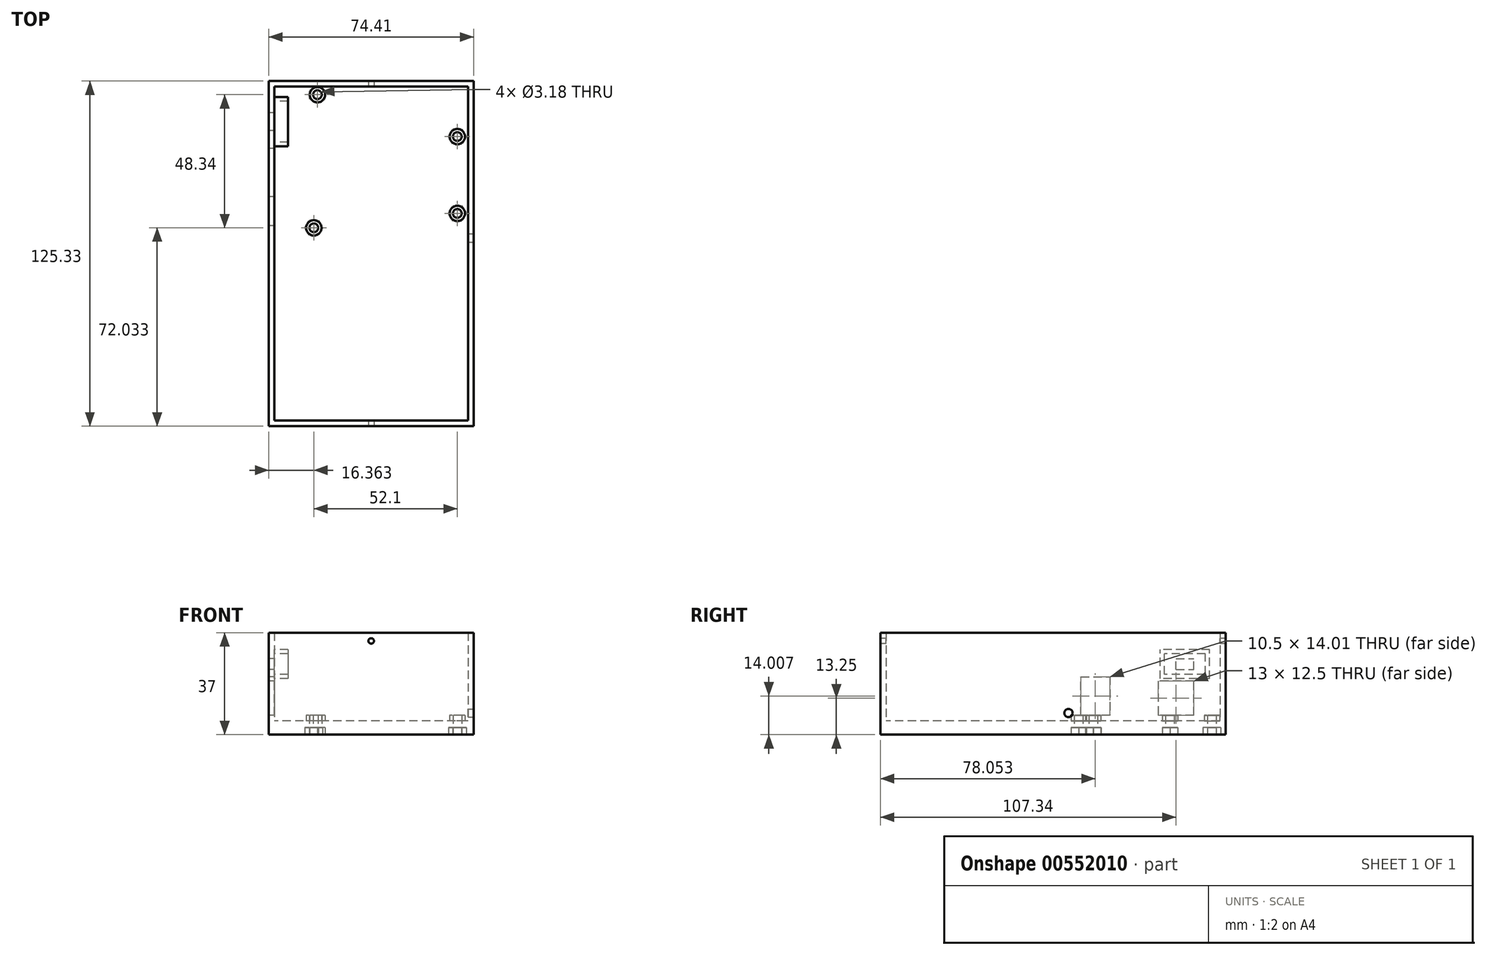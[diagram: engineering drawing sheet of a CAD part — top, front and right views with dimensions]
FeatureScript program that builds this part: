
annotation { "Feature Type Name" : "Feature", "Feature Type Description" : "" }
export const myFeature = defineFeature(function(context is Context, id is Id, definition is map)
    precondition{}
    {
        {
            var Q0;
            Q0=qCreatedBy(makeId("Top.planeOp"),FACE);
            var sketch = newSketch(context, id + "F0", { "sketchPlane" : qUnion([Q0])});
            skLineSegment(sketch, "E0.right", {"start": v(-46.5, 29) * mm, "end": v(-46.5, -29) * mm});
            skPoint(sketch, "E0.middle", {"position": v(0, 0) * mm});
            skCircle(sketch, "E1", {"center": v(-30.14, -24.3) * mm, "radius": 1.59 * mm});
            skCircle(sketch, "E2", {"center": v(21.96, -19.06) * mm, "radius": 1.59 * mm});
            skCircle(sketch, "E3", {"center": v(21.96, 8.84) * mm, "radius": 1.59 * mm});
            skCircle(sketch, "E4", {"center": v(-28.84, 24.04) * mm, "radius": 1.59 * mm});
            skLineSegment(sketch, "E5.left", {"start": v(-46.5, -29) * mm, "end": v(-46.5, -29) * mm});
            skLineSegment(sketch, "E6.right", {"start": v(-46.5, -29) * mm, "end": v(-46.5, -96.33) * mm});
            skLineSegment(sketch, "E7", {"start": v(27.91, 29) * mm, "end": v(27.91, -96.33) * mm});
            skLineSegment(sketch, "E8", {"start": v(-46.5, 29) * mm, "end": v(27.91, 29) * mm});
            skLineSegment(sketch, "E9", {"start": v(27.91, -96.33) * mm, "end": v(-46.5, -96.33) * mm});
            skSolve(sketch);
        }
        {
            var Q0;
            Q0=makeQuery(id+"F0.imprint","IMPRINT",FACE,{"disambiguationData":[TD([[makeQuery(id+"F0.imprint","IMPRINT",EDGE,{"derivedFrom":sQuery(id+"F0.wireOp",EDGE,"E0.bottom")}),1.0]])]});
            var Q1;
            Q1=makeQuery(id+"F0.imprint","IMPRINT",FACE,{"disambiguationData":[TD([[makeQuery(id+"F0.imprint","IMPRINT",EDGE,{"derivedFrom":sQuery(id+"F0.wireOp",EDGE,"E2")}),1.0]])]});
            var Q2;
            Q2=makeQuery(id+"F0.imprint","IMPRINT",FACE,{"disambiguationData":[TD([[makeQuery(id+"F0.imprint","IMPRINT",EDGE,{"derivedFrom":sQuery(id+"F0.wireOp",EDGE,"E4")}),1.0]])]});
            var Q3;
            Q3=makeQuery(id+"F0.imprint","IMPRINT",FACE,{"disambiguationData":[TD([[makeQuery(id+"F0.imprint","IMPRINT",EDGE,{"derivedFrom":sQuery(id+"F0.wireOp",EDGE,"E1")}),1.0]])]});
            var Q4;
            Q4=makeQuery(id+"F0.imprint","IMPRINT",FACE,{"disambiguationData":[TD([[makeQuery(id+"F0.imprint","IMPRINT",EDGE,{"derivedFrom":sQuery(id+"F0.wireOp",EDGE,"E3")}),1.0]])]});
            var Q5;
            Q5=makeQuery(id+"F0.imprint","IMPRINT",FACE,{"disambiguationData":[TD([[makeQuery(id+"F0.imprint","IMPRINT",EDGE,{"derivedFrom":sQuery(id+"F0.wireOp",EDGE,"E6.bottom")}),1.0]])]});
            var Q6;
            Q6=makeQuery(id+"F0.imprint","IMPRINT",FACE,{"disambiguationData":[TD([[makeQuery(id+"F0.imprint","IMPRINT",EDGE,{"derivedFrom":sQuery(id+"F0.wireOp",EDGE,"E0.right")}),1.0]])]});
            extrude(context, id + "F1", {"entities" : qUnion([Q0, Q1, Q2, Q3, Q4, Q5, Q6]), "depth" : 5 * mm, "offsetDistance" : 25 * mm});
        }
        {
            var Q0;
            Q0=makeQuery(id+"F1.opExtrude","CAP_FACE",FACE,{"disambiguationData":[OSD([sQuery(id+"F0.wireOp",EDGE,"E0.bottom"),sQuery(id+"F0.wireOp",EDGE,"E0.top"),sQuery(id+"F0.wireOp",EDGE,"E0.left"),sQuery(id+"F0.wireOp",EDGE,"E0.right"),sQuery(id+"F0.wireOp",EDGE,"E1"),sQuery(id+"F0.wireOp",EDGE,"E2"),sQuery(id+"F0.wireOp",EDGE,"E3"),sQuery(id+"F0.wireOp",EDGE,"E4")])],"isStart":false});
            var sketch = newSketch(context, id + "F2", { "sketchPlane" : qUnion([Q0])});
            skLineSegment(sketch, "E10.0", {"start": v(25.91, -94.33) * mm, "end": v(-44.5, -94.33) * mm});
            skLineSegment(sketch, "E10.1", {"start": v(25.91, 27) * mm, "end": v(25.91, -94.33) * mm});
            skLineSegment(sketch, "E10.2", {"start": v(-44.5, -29) * mm, "end": v(-44.5, -94.33) * mm});
            skLineSegment(sketch, "E10.3", {"start": v(-44.5, 27) * mm, "end": v(-44.5, -29) * mm});
            skLineSegment(sketch, "E10.4", {"start": v(-44.5, 27) * mm, "end": v(25.91, 27) * mm});
            skSolve(sketch);
        }
        {
            var Q0;
            Q0=makeQuery(id+"F2.imprint","IMPRINT",FACE,{"disambiguationData":[TD([[makeQuery(id+"F2.imprint","IMPRINT",EDGE,{"derivedFrom":sQuery(id+"F2.wireOp",EDGE,"E10.0")}),1.0]])]});
            extrude(context, id + "F3", {"entities" : qUnion([Q0]), "operationType" : NewBodyOperationType.ADD, "depth" : 32 * mm, "offsetDistance" : 25 * mm});
        }
        {
            var Q0;
            Q0=makeQuery(id+"F1.opExtrude","CAP_FACE",FACE,{"disambiguationData":[OSD([sQuery(id+"F0.wireOp",EDGE,"E0.bottom"),sQuery(id+"F0.wireOp",EDGE,"E0.top"),sQuery(id+"F0.wireOp",EDGE,"E0.left"),sQuery(id+"F0.wireOp",EDGE,"E0.right"),sQuery(id+"F0.wireOp",EDGE,"E1"),sQuery(id+"F0.wireOp",EDGE,"E2"),sQuery(id+"F0.wireOp",EDGE,"E3"),sQuery(id+"F0.wireOp",EDGE,"E4")])],"isStart":false});
            var sketch = newSketch(context, id + "F4", { "sketchPlane" : qUnion([Q0])});
            skCircle(sketch, "E11.0", {"center": v(-28.84, 24.04) * mm, "radius": 2.8 * mm});
            skCircle(sketch, "E12.0", {"center": v(21.96, 8.84) * mm, "radius": 2.79 * mm});
            skCircle(sketch, "E13.0", {"center": v(21.96, -19.06) * mm, "radius": 2.8 * mm});
            skCircle(sketch, "E14.0", {"center": v(-30.14, -24.3) * mm, "radius": 2.8 * mm});
            skSolve(sketch);
        }
        {
            var Q0;
            Q0 = qSketchRegion(id + "F4", true);
            extrude(context, id + "F5", {"entities" : qUnion([Q0]), "operationType" : NewBodyOperationType.ADD, "depth" : 2 * mm, "offsetDistance" : 25 * mm});
        }
        {
            var Q0;
            Q0=makeQuery(id+"F0.imprint","IMPRINT",FACE,{"disambiguationData":[TD([[makeQuery(id+"F0.imprint","IMPRINT",EDGE,{"derivedFrom":sQuery(id+"F0.wireOp",EDGE,"E1")}),1.0]])]});
            var Q1;
            Q1=makeQuery(id+"F0.imprint","IMPRINT",FACE,{"disambiguationData":[TD([[makeQuery(id+"F0.imprint","IMPRINT",EDGE,{"derivedFrom":sQuery(id+"F0.wireOp",EDGE,"E2")}),1.0]])]});
            var Q2;
            Q2=makeQuery(id+"F0.imprint","IMPRINT",FACE,{"disambiguationData":[TD([[makeQuery(id+"F0.imprint","IMPRINT",EDGE,{"derivedFrom":sQuery(id+"F0.wireOp",EDGE,"E3")}),1.0]])]});
            var Q3;
            Q3=makeQuery(id+"F0.imprint","IMPRINT",FACE,{"disambiguationData":[TD([[makeQuery(id+"F0.imprint","IMPRINT",EDGE,{"derivedFrom":sQuery(id+"F0.wireOp",EDGE,"E4")}),1.0]])]});
            var Q4;
            Q4=sQuery(id+"F0.wireOp",EDGE,"E1");
            var Q5;
            Q5=sQuery(id+"F0.wireOp",EDGE,"E2");
            var Q6;
            Q6=sQuery(id+"F0.wireOp",EDGE,"E3");
            var Q7;
            Q7=sQuery(id+"F0.wireOp",EDGE,"E4");
            extrude(context, id + "F6", {"entities" : qUnion([Q0, Q1, Q2, Q3]), "operationType" : NewBodyOperationType.REMOVE, "surfaceEntities" : qUnion([Q4, Q5, Q6, Q7]), "endBound" : BoundingType.THROUGH_ALL, "depth" : 25 * mm, "offsetDistance" : 25 * mm});
        }
        {
            var Q0;
            Q0=qCreatedBy(makeId("Top.planeOp"),FACE);
            var sketch = newSketch(context, id + "F7", { "sketchPlane" : qUnion([Q0])});
            skCircle(sketch, "E15.cCircle", {"center": v(-30.14, -24.3) * mm, "radius": 2.8 * mm, "construction": true});
            skLineSegment(sketch, "E15.0", {"start": v(-26.9, -24.32) * mm, "end": v(-28.54, -27.1) * mm});
            skLineSegment(sketch, "E15.1", {"start": v(-28.54, -27.1) * mm, "end": v(-31.77, -27.09) * mm});
            skLineSegment(sketch, "E15.2", {"start": v(-31.77, -27.09) * mm, "end": v(-33.37, -24.28) * mm});
            skLineSegment(sketch, "E15.3", {"start": v(-33.37, -24.28) * mm, "end": v(-31.73, -21.49) * mm});
            skLineSegment(sketch, "E15.4", {"start": v(-31.73, -21.49) * mm, "end": v(-28.5, -21.5) * mm});
            skLineSegment(sketch, "E15.5", {"start": v(-28.5, -21.5) * mm, "end": v(-26.9, -24.32) * mm});
            skPoint(sketch, "E15.0.midPoint", {"position": v(-27.72, -25.71) * mm});
            skCircle(sketch, "E16.cCircle", {"center": v(21.96, -19.06) * mm, "radius": 2.8 * mm, "construction": true});
            skLineSegment(sketch, "E16.0", {"start": v(25.2, -18.98) * mm, "end": v(23.65, -21.82) * mm});
            skLineSegment(sketch, "E16.1", {"start": v(23.65, -21.82) * mm, "end": v(20.42, -21.9) * mm});
            skLineSegment(sketch, "E16.2", {"start": v(20.42, -21.9) * mm, "end": v(18.73, -19.14) * mm});
            skLineSegment(sketch, "E16.3", {"start": v(18.73, -19.14) * mm, "end": v(20.28, -16.3) * mm});
            skLineSegment(sketch, "E16.4", {"start": v(20.28, -16.3) * mm, "end": v(23.5, -16.22) * mm});
            skLineSegment(sketch, "E16.5", {"start": v(23.5, -16.22) * mm, "end": v(25.2, -18.98) * mm});
            skPoint(sketch, "E16.0.midPoint", {"position": v(24.42, -20.4) * mm});
            skCircle(sketch, "E17.cCircle", {"center": v(21.96, 8.84) * mm, "radius": 2.8 * mm, "construction": true});
            skLineSegment(sketch, "E17.0", {"start": v(25.2, 8.84) * mm, "end": v(23.58, 6.04) * mm});
            skLineSegment(sketch, "E17.1", {"start": v(23.58, 6.04) * mm, "end": v(20.34, 6.05) * mm});
            skLineSegment(sketch, "E17.2", {"start": v(20.34, 6.05) * mm, "end": v(18.73, 8.85) * mm});
            skLineSegment(sketch, "E17.3", {"start": v(18.73, 8.85) * mm, "end": v(20.35, 11.65) * mm});
            skLineSegment(sketch, "E17.4", {"start": v(20.35, 11.65) * mm, "end": v(23.58, 11.64) * mm});
            skLineSegment(sketch, "E17.5", {"start": v(23.58, 11.64) * mm, "end": v(25.2, 8.84) * mm});
            skPoint(sketch, "E17.0.midPoint", {"position": v(24.39, 7.44) * mm});
            skCircle(sketch, "E18.cCircle", {"center": v(-28.84, 24.04) * mm, "radius": 3.23 * mm, "construction": true});
            skLineSegment(sketch, "E18.0", {"start": v(-26.04, 22.43) * mm, "end": v(-28.84, 20.8) * mm});
            skLineSegment(sketch, "E18.1", {"start": v(-28.84, 20.8) * mm, "end": v(-31.64, 22.43) * mm});
            skLineSegment(sketch, "E18.2", {"start": v(-31.64, 22.43) * mm, "end": v(-31.64, 25.66) * mm});
            skLineSegment(sketch, "E18.3", {"start": v(-31.64, 25.66) * mm, "end": v(-28.84, 27.28) * mm});
            skLineSegment(sketch, "E18.4", {"start": v(-28.84, 27.28) * mm, "end": v(-26.04, 25.66) * mm});
            skLineSegment(sketch, "E18.5", {"start": v(-26.04, 25.66) * mm, "end": v(-26.04, 22.43) * mm});
            skSolve(sketch);
        }
        {
            var Q0;
            Q0 = qSketchRegion(id + "F7", true);
            extrude(context, id + "F8", {"entities" : qUnion([Q0]), "operationType" : NewBodyOperationType.REMOVE, "depth" : 2.6 * mm, "offsetDistance" : 25 * mm});
        }
        {
            var Q0;
            {var subQ0=sQuery(id+"F0.wireOp",EDGE,"E6.right");var subQ1=sQuery(id+"F0.wireOp",EDGE,"E0.right");Q0=makeQuery(id+"F3.boolean.opBoolean","MERGE",FACE,{"derivedFrom":[makeQuery(id+"F1.opExtrude","SWEPT_FACE",FACE,{"disambiguationData":[OSD([subQ1,subQ0])]}),makeQuery(id+"F3.opExtrude","SWEPT_FACE",FACE,{"disambiguationData":[OSD([subQ1,subQ0])]})]});}
            var sketch = newSketch(context, id + "F9", { "sketchPlane" : qUnion([Q0])});
            skLineSegment(sketch, "E19", {"start": v(-23.91, 0) * mm, "end": v(-17.51, 0) * mm, "construction": true});
            skLineSegment(sketch, "E20", {"start": v(-17.51, 0) * mm, "end": v(-4.51, 0) * mm});
            skLineSegment(sketch, "E21", {"start": v(-4.51, 0) * mm, "end": v(-4.51, 19.5) * mm});
            skLineSegment(sketch, "E22", {"start": v(-4.51, 19.5) * mm, "end": v(-17.51, 19.5) * mm});
            skLineSegment(sketch, "E23", {"start": v(-17.51, 19.5) * mm, "end": v(-17.51, 0) * mm});
            skLineSegment(sketch, "E24", {"start": v(-4.51, 0) * mm, "end": v(-4.51, 7) * mm, "construction": true});
            skLineSegment(sketch, "E25", {"start": v(-4.51, 7) * mm, "end": v(-17.51, 7) * mm});
            skLineSegment(sketch, "E26", {"start": v(24.53, 0) * mm, "end": v(23.53, 0) * mm, "construction": true});
            skLineSegment(sketch, "E27", {"start": v(23.53, 0) * mm, "end": v(23.53, 7) * mm, "construction": true});
            skLineSegment(sketch, "E28", {"start": v(23.53, 7) * mm, "end": v(13.03, 7) * mm});
            skLineSegment(sketch, "E29", {"start": v(13.03, 7) * mm, "end": v(13.03, 21.01) * mm});
            skLineSegment(sketch, "E30", {"start": v(13.03, 21.01) * mm, "end": v(23.53, 21.01) * mm});
            skLineSegment(sketch, "E31", {"start": v(23.53, 21.01) * mm, "end": v(23.53, 7) * mm});
            skLineSegment(sketch, "E32.bottom", {"start": v(-17.51, 27.6) * mm, "end": v(-11.01, 27.6) * mm});
            skLineSegment(sketch, "E32.top", {"start": v(-17.51, 23.6) * mm, "end": v(-11.01, 23.6) * mm});
            skLineSegment(sketch, "E32.left", {"start": v(-17.51, 27.6) * mm, "end": v(-17.51, 23.6) * mm});
            skLineSegment(sketch, "E32.right", {"start": v(-11.01, 27.6) * mm, "end": v(-11.01, 23.6) * mm});
            skLineSegment(sketch, "E33", {"start": v(-11.01, 27.6) * mm, "end": v(-17.51, 23.6) * mm, "construction": true});
            skLineSegment(sketch, "E34.bottom", {"start": v(-6.86, 29.3) * mm, "end": v(-21.66, 29.3) * mm});
            skLineSegment(sketch, "E34.top", {"start": v(-6.86, 21.9) * mm, "end": v(-21.66, 21.9) * mm});
            skLineSegment(sketch, "E34.left", {"start": v(-6.86, 29.3) * mm, "end": v(-6.86, 21.9) * mm});
            skLineSegment(sketch, "E34.right", {"start": v(-21.66, 29.3) * mm, "end": v(-21.66, 21.9) * mm});
            skPoint(sketch, "E34.middle", {"position": v(-14.26, 25.6) * mm});
            skLineSegment(sketch, "E35.0", {"start": v(-5.26, 30.9) * mm, "end": v(-5.26, 20.3) * mm});
            skLineSegment(sketch, "E35.1", {"start": v(-5.26, 30.9) * mm, "end": v(-23.26, 30.9) * mm});
            skLineSegment(sketch, "E35.2", {"start": v(-23.26, 30.9) * mm, "end": v(-23.26, 20.3) * mm});
            skLineSegment(sketch, "E35.3", {"start": v(-5.26, 20.3) * mm, "end": v(-23.26, 20.3) * mm});
            skSolve(sketch);
        }
        {
            var Q0;
            {var subQ0=sQuery(id+"F9.wireOp",EDGE,"E22");Q0=makeQuery(id+"F9.imprint","IMPRINT",FACE,{"disambiguationData":[TD([[makeQuery(id+"F9.imprint","IMPRINT",EDGE,{"derivedFrom":subQ0}),1.0]])]});}
            var Q1;
            Q1=makeQuery(id+"F9.imprint","IMPRINT",FACE,{"disambiguationData":[TD([[makeQuery(id+"F9.imprint","IMPRINT",EDGE,{"derivedFrom":sQuery(id+"F9.wireOp",EDGE,"E28")}),-1.0]])]});
            var Q2;
            Q2=makeQuery(id+"F9.imprint","IMPRINT",FACE,{"disambiguationData":[TD([[makeQuery(id+"F9.imprint","IMPRINT",EDGE,{"derivedFrom":sQuery(id+"F9.wireOp",EDGE,"E32.bottom")}),-1.0]])]});
            extrude(context, id + "F10", {"entities" : qUnion([Q0, Q1, Q2]), "operationType" : NewBodyOperationType.REMOVE, "oppositeDirection" : true, "depth" : 3 * mm, "offsetDistance" : 25 * mm});
        }
        {
            var Q0;
            Q0=makeQuery(id+"F9.imprint","IMPRINT",FACE,{"disambiguationData":[TD([[makeQuery(id+"F9.imprint","IMPRINT",EDGE,{"derivedFrom":sQuery(id+"F9.wireOp",EDGE,"E34.bottom")}),-1.0]])]});
            extrude(context, id + "F11", {"entities" : qUnion([Q0]), "operationType" : NewBodyOperationType.ADD, "oppositeDirection" : true, "depth" : 7 * mm, "offsetDistance" : 25 * mm});
        }
        {
            var Q0;
            Q0=makeQuery(id+"F1.opExtrude","CAP_FACE",FACE,{"disambiguationData":[OSD([sQuery(id+"F0.wireOp",EDGE,"E0.right"),sQuery(id+"F0.wireOp",EDGE,"E6.right"),sQuery(id+"F0.wireOp",EDGE,"E7"),sQuery(id+"F0.wireOp",EDGE,"E8"),sQuery(id+"F0.wireOp",EDGE,"E9")])],"isStart":false});
            var sketch = newSketch(context, id + "F12", { "sketchPlane" : qUnion([Q0])});
            skLineSegment(sketch, "E36.bottom", {"start": v(-40.75, -18.45) * mm, "end": v(-10.75, -18.45) * mm});
            skLineSegment(sketch, "E36.top", {"start": v(-40.75, -15.95) * mm, "end": v(-10.75, -15.95) * mm});
            skLineSegment(sketch, "E37.bottom", {"start": v(-40.75, -13.79) * mm, "end": v(-10.75, -13.79) * mm});
            skLineSegment(sketch, "E37.top", {"start": v(-40.75, -11.29) * mm, "end": v(-10.75, -11.29) * mm});
            skLineSegment(sketch, "E38.bottom", {"start": v(-40.75, -9.18) * mm, "end": v(-10.75, -9.18) * mm});
            skLineSegment(sketch, "E38.top", {"start": v(-40.75, -6.68) * mm, "end": v(-10.75, -6.68) * mm});
            skLineSegment(sketch, "E39.bottom", {"start": v(-40.75, -4.6) * mm, "end": v(-10.75, -4.6) * mm});
            skLineSegment(sketch, "E39.top", {"start": v(-40.75, -2.1) * mm, "end": v(-10.75, -2.1) * mm});
            skLineSegment(sketch, "E40.bottom", {"start": v(-40.75, 0) * mm, "end": v(-10.75, 0) * mm});
            skLineSegment(sketch, "E40.top", {"start": v(-40.75, 2.5) * mm, "end": v(-10.75, 2.5) * mm});
            skLineSegment(sketch, "E41.bottom", {"start": v(-40.75, 4.14) * mm, "end": v(-10.75, 4.14) * mm});
            skLineSegment(sketch, "E41.top", {"start": v(-40.75, 6.64) * mm, "end": v(-10.75, 6.64) * mm});
            skLineSegment(sketch, "E42.bottom", {"start": v(-40.75, 8.51) * mm, "end": v(-10.75, 8.51) * mm});
            skLineSegment(sketch, "E42.top", {"start": v(-40.75, 11.01) * mm, "end": v(-10.75, 11.01) * mm});
            skLineSegment(sketch, "E43.bottom", {"start": v(-40.75, 12.99) * mm, "end": v(-10.75, 12.99) * mm});
            skLineSegment(sketch, "E43.top", {"start": v(-40.75, 15.49) * mm, "end": v(-10.75, 15.49) * mm});
            skLineSegment(sketch, "E44.bottom", {"start": v(-40.75, 17.25) * mm, "end": v(-10.75, 17.25) * mm});
            skLineSegment(sketch, "E44.top", {"start": v(-40.75, 19.75) * mm, "end": v(-10.75, 19.75) * mm});
            skArc(sketch, "E45", {"start": v(-10.75, 17.25) * mm, "mid": v(-9.5, 18.5) * mm, "end": v(-10.75, 19.75) * mm});
            skArc(sketch, "E46", {"start": v(-10.75, 12.99) * mm, "mid": v(-9.5, 14.24) * mm, "end": v(-10.75, 15.49) * mm});
            skArc(sketch, "E47", {"start": v(-10.75, 8.51) * mm, "mid": v(-9.5, 9.76) * mm, "end": v(-10.75, 11.01) * mm});
            skArc(sketch, "E48", {"start": v(-10.75, 4.14) * mm, "mid": v(-9.5, 5.4) * mm, "end": v(-10.75, 6.64) * mm});
            skPoint(sketch, "E48.midSnap0", {"position": v(-10.75, 5.4) * mm});
            skArc(sketch, "E49", {"start": v(-10.75, 0) * mm, "mid": v(-9.5, 1.25) * mm, "end": v(-10.75, 2.5) * mm});
            skArc(sketch, "E50", {"start": v(-10.75, -4.6) * mm, "mid": v(-9.5, -3.34) * mm, "end": v(-10.75, -2.1) * mm});
            skArc(sketch, "E51", {"start": v(-10.75, -9.18) * mm, "mid": v(-9.5, -7.93) * mm, "end": v(-10.75, -6.68) * mm});
            skArc(sketch, "E52", {"start": v(-10.75, -13.79) * mm, "mid": v(-9.5, -12.54) * mm, "end": v(-10.75, -11.29) * mm});
            skArc(sketch, "E53", {"start": v(-10.75, -18.45) * mm, "mid": v(-9.5, -17.2) * mm, "end": v(-10.75, -15.95) * mm});
            skArc(sketch, "E54", {"start": v(-40.75, -15.95) * mm, "mid": v(-42, -17.2) * mm, "end": v(-40.75, -18.45) * mm});
            skArc(sketch, "E55", {"start": v(-40.75, -11.29) * mm, "mid": v(-42, -12.54) * mm, "end": v(-40.75, -13.79) * mm});
            skArc(sketch, "E56", {"start": v(-40.75, -6.68) * mm, "mid": v(-42, -7.93) * mm, "end": v(-40.75, -9.18) * mm});
            skArc(sketch, "E57", {"start": v(-40.75, -2.1) * mm, "mid": v(-42, -3.34) * mm, "end": v(-40.75, -4.6) * mm});
            skArc(sketch, "E58", {"start": v(-40.75, 2.5) * mm, "mid": v(-42, 1.25) * mm, "end": v(-40.75, 0) * mm});
            skArc(sketch, "E59", {"start": v(-40.75, 6.64) * mm, "mid": v(-42, 5.4) * mm, "end": v(-40.75, 4.14) * mm});
            skArc(sketch, "E60", {"start": v(-40.75, 11.01) * mm, "mid": v(-42, 9.76) * mm, "end": v(-40.75, 8.51) * mm});
            skArc(sketch, "E61", {"start": v(-40.75, 15.49) * mm, "mid": v(-42, 14.24) * mm, "end": v(-40.75, 12.99) * mm});
            skArc(sketch, "E62", {"start": v(-40.75, 19.75) * mm, "mid": v(-42, 18.5) * mm, "end": v(-40.75, 17.25) * mm});
            skSolve(sketch);
        }
        {
            var Q0;
            Q0=makeQuery(id+"F12.imprint","IMPRINT",FACE,{"disambiguationData":[TD([[makeQuery(id+"F12.imprint","IMPRINT",EDGE,{"derivedFrom":sQuery(id+"F12.wireOp",EDGE,"E40.bottom")}),1.0]])]});
            var Q1;
            Q1=makeQuery(id+"F12.imprint","IMPRINT",FACE,{"disambiguationData":[TD([[makeQuery(id+"F12.imprint","IMPRINT",EDGE,{"derivedFrom":sQuery(id+"F12.wireOp",EDGE,"E39.bottom")}),1.0]])]});
            var Q2;
            Q2=makeQuery(id+"F12.imprint","IMPRINT",FACE,{"disambiguationData":[TD([[makeQuery(id+"F12.imprint","IMPRINT",EDGE,{"derivedFrom":sQuery(id+"F12.wireOp",EDGE,"E38.bottom")}),1.0]])]});
            var Q3;
            Q3=makeQuery(id+"F12.imprint","IMPRINT",FACE,{"disambiguationData":[TD([[makeQuery(id+"F12.imprint","IMPRINT",EDGE,{"derivedFrom":sQuery(id+"F12.wireOp",EDGE,"E37.bottom")}),1.0]])]});
            var Q4;
            Q4=makeQuery(id+"F12.imprint","IMPRINT",FACE,{"disambiguationData":[TD([[makeQuery(id+"F12.imprint","IMPRINT",EDGE,{"derivedFrom":sQuery(id+"F12.wireOp",EDGE,"E36.bottom")}),1.0]])]});
            var Q5;
            Q5=makeQuery(id+"F12.imprint","IMPRINT",FACE,{"disambiguationData":[TD([[makeQuery(id+"F12.imprint","IMPRINT",EDGE,{"derivedFrom":sQuery(id+"F12.wireOp",EDGE,"E41.bottom")}),1.0]])]});
            var Q6;
            Q6=makeQuery(id+"F12.imprint","IMPRINT",FACE,{"disambiguationData":[TD([[makeQuery(id+"F12.imprint","IMPRINT",EDGE,{"derivedFrom":sQuery(id+"F12.wireOp",EDGE,"E42.bottom")}),1.0]])]});
            var Q7;
            Q7=makeQuery(id+"F12.imprint","IMPRINT",FACE,{"disambiguationData":[TD([[makeQuery(id+"F12.imprint","IMPRINT",EDGE,{"derivedFrom":sQuery(id+"F12.wireOp",EDGE,"E43.bottom")}),1.0]])]});
            var Q8;
            Q8=makeQuery(id+"F12.imprint","IMPRINT",FACE,{"disambiguationData":[TD([[makeQuery(id+"F12.imprint","IMPRINT",EDGE,{"derivedFrom":sQuery(id+"F12.wireOp",EDGE,"E44.bottom")}),1.0]])]});
            extrude(context, id + "F13", {"entities" : qUnion([Q0, Q1, Q2, Q3, Q4, Q5, Q6, Q7, Q8]), "operationType" : NewBodyOperationType.REMOVE, "depth" : 6 * mm, "offsetDistance" : 25 * mm});
        }
        {
            var Q0;
            {var subQ0=sQuery(id+"F0.wireOp",EDGE,"E9");Q0=makeQuery(id+"F3.boolean.opBoolean","MERGE",FACE,{"derivedFrom":[makeQuery(id+"F1.opExtrude","SWEPT_FACE",FACE,{"disambiguationData":[OSD([subQ0])]}),makeQuery(id+"F3.opExtrude","SWEPT_FACE",FACE,{"disambiguationData":[OSD([subQ0])]})]});}
            var sketch = newSketch(context, id + "F14", { "sketchPlane" : qUnion([Q0])});
            skCircle(sketch, "E63", {"center": v(-9.3, 34) * mm, "radius": 1 * mm});
            skPoint(sketch, "E63.centerSnap0", {"position": v(-9.3, 37) * mm});
            skSolve(sketch);
        }
        {
            var Q0;
            Q0=makeQuery(id+"F14.imprint","IMPRINT",FACE,{"disambiguationData":[TD([[makeQuery(id+"F14.imprint","IMPRINT",EDGE,{"derivedFrom":sQuery(id+"F14.wireOp",EDGE,"E63")}),1.0]])]});
            var Q1;
            Q1=sQuery(id+"F14.wireOp",EDGE,"E63");
            extrude(context, id + "F15", {"entities" : qUnion([Q0]), "operationType" : NewBodyOperationType.REMOVE, "surfaceEntities" : qUnion([Q1]), "endBound" : BoundingType.THROUGH_ALL, "oppositeDirection" : true, "depth" : 25 * mm, "offsetDistance" : 25 * mm});
        }
        {
            var Q0;
            {var subQ0=sQuery(id+"F0.wireOp",EDGE,"E7");Q0=makeQuery(id+"F3.boolean.opBoolean","MERGE",FACE,{"derivedFrom":[makeQuery(id+"F1.opExtrude","SWEPT_FACE",FACE,{"disambiguationData":[OSD([subQ0])]}),makeQuery(id+"F3.opExtrude","SWEPT_FACE",FACE,{"disambiguationData":[OSD([subQ0])]})]});}
            var sketch = newSketch(context, id + "F16", { "sketchPlane" : qUnion([Q0])});
            skCircle(sketch, "E64", {"center": v(-28, 7.83) * mm, "radius": 1.5 * mm});
            skSolve(sketch);
        }
        {
            var Q0;
            Q0=makeQuery(id+"F16.imprint","IMPRINT",FACE,{"disambiguationData":[TD([[makeQuery(id+"F16.imprint","IMPRINT",EDGE,{"derivedFrom":sQuery(id+"F16.wireOp",EDGE,"E64")}),1.0]])]});
            var Q1;
            Q1=sQuery(id+"F16.wireOp",EDGE,"E64");
            extrude(context, id + "F17", {"entities" : qUnion([Q0]), "operationType" : NewBodyOperationType.REMOVE, "surfaceEntities" : qUnion([Q1]), "oppositeDirection" : true, "depth" : 3 * mm, "offsetDistance" : 25 * mm});
        }
    });
